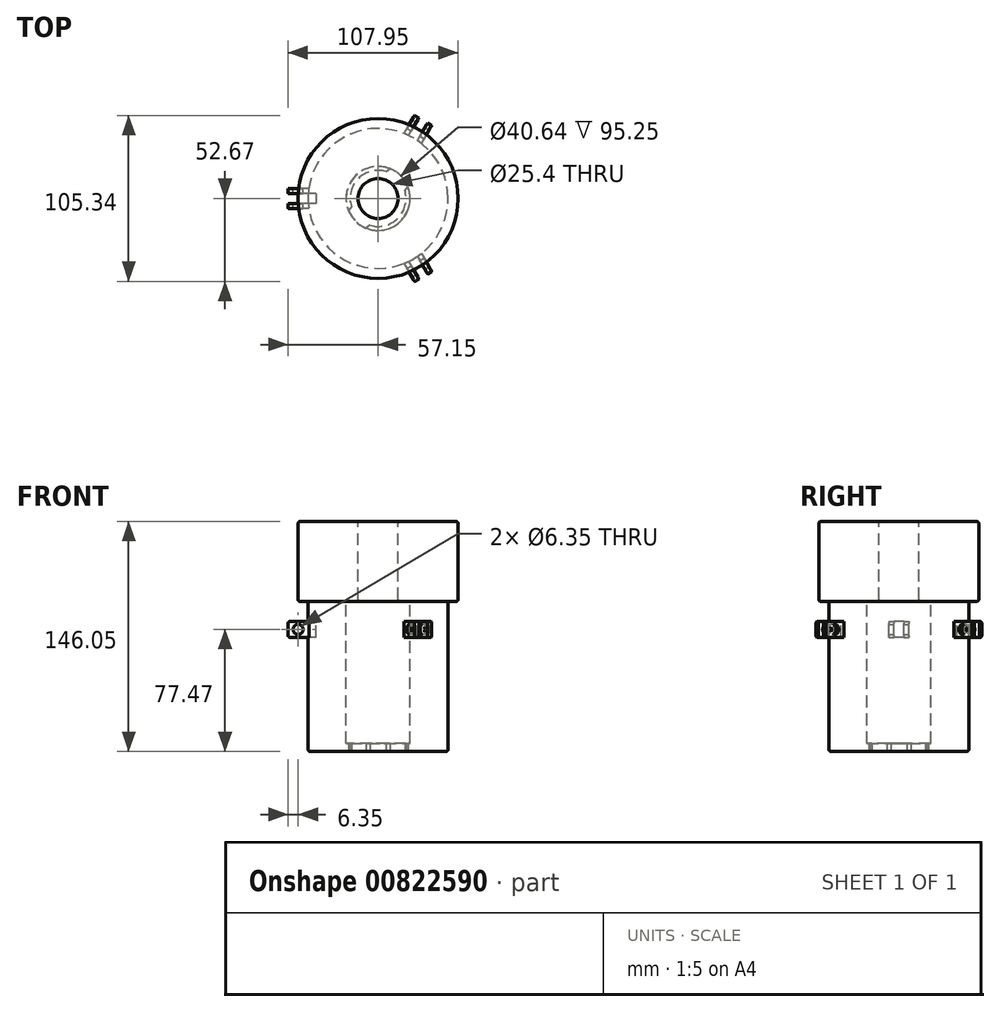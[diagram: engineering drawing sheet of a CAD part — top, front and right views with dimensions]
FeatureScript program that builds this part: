
annotation { "Feature Type Name" : "Feature", "Feature Type Description" : "" }
export const myFeature = defineFeature(function(context is Context, id is Id, definition is map)
    precondition{}
    {
        {
            var Q0;
            Q0=qCreatedBy(makeId("Top.planeOp"),FACE);
            var sketch = newSketch(context, id + "F0", { "sketchPlane" : qUnion([Q0])});
            skCircle(sketch, "E0", {"center": v(0, 0) * mm, "radius": 20.32 * mm});
            skCircle(sketch, "E1", {"center": v(0, 0) * mm, "radius": 44.45 * mm});
            skSolve(sketch);
        }
        {
            var Q0;
            Q0 = qSketchRegion(id + "F0", true);
            extrude(context, id + "F1", {"entities" : qUnion([Q0]), "oppositeDirection" : true, "depth" : 95.25 * mm, "offsetDistance" : 25.4 * mm});
        }
        {
            var Q0;
            Q0=makeQuery(id+"F0.imprint","IMPRINT",FACE,{"disambiguationData":[TD([[makeQuery(id+"F0.imprint","IMPRINT",EDGE,{"derivedFrom":sQuery(id+"F0.wireOp",EDGE,"E0")}),1.0]])]});
            var Q1;
            Q1=makeQuery(id+"F1.opExtrude","CAP_FACE",FACE,{"disambiguationData":[OSD([sQuery(id+"F0.wireOp",EDGE,"E0"),sQuery(id+"F0.wireOp",EDGE,"E1")])],"isStart":false});
            extrude(context, id + "F2", {"entities" : qUnion([Q0]), "operationType" : NewBodyOperationType.REMOVE, "depth" : 25.4 * mm, "endBoundEntityFace" : qUnion([Q1]), "offsetDistance" : 25.4 * mm});
        }
        {
            var Q0;
            {var subQ0=sQuery(id+"F0.wireOp",EDGE,"E0");Q0=makeQuery(id+"F2.boolean.opBoolean","MERGE",FACE,{"derivedFrom":[makeQuery(id+"F1.opExtrude","CAP_FACE",FACE,{"disambiguationData":[OSD([subQ0,sQuery(id+"F0.wireOp",EDGE,"E1")])],"isStart":true}),makeQuery(id+"F2.opExtrude","CAP_FACE",FACE,{"disambiguationData":[OSD([subQ0])],"isStart":true})]});}
            var sketch = newSketch(context, id + "F3", { "sketchPlane" : qUnion([Q0])});
            skCircle(sketch, "E2", {"center": v(0, 0) * mm, "radius": 50.8 * mm});
            skSolve(sketch);
        }
        {
            var Q0;
            Q0 = qSketchRegion(id + "F3", true);
            extrude(context, id + "F4", {"entities" : qUnion([Q0]), "operationType" : NewBodyOperationType.ADD, "depth" : 50.8 * mm, "offsetDistance" : 25.4 * mm});
        }
        {
            var Q0;
            Q0=makeQuery(id+"F4.opExtrude","SWEPT_FACE",FACE,{"disambiguationData":[OSD([sQuery(id+"F3.wireOp",EDGE,"E2")])]});
            fillet(context, id + "F5", {"entities" : qUnion([Q0]), "radius" : 1.27 * mm, "tangentPropagation" : true, "allowEdgeOverflow" : false});
        }
        {
            var Q0;
            Q0=makeQuery(id+"F1.opExtrude","CAP_EDGE",EDGE,{"disambiguationData":[OSD([sQuery(id+"F0.wireOp",EDGE,"E1")])],"isStart":false});
            fillet(context, id + "F6", {"entities" : qUnion([Q0]), "radius" : 1.27 * mm, "tangentPropagation" : true, "allowEdgeOverflow" : false});
        }
        {
            var Q0;
            Q0=makeQuery(id+"F4.opExtrude","CAP_FACE",FACE,{"disambiguationData":[OSD([sQuery(id+"F3.wireOp",EDGE,"E2")])],"isStart":false});
            var sketch = newSketch(context, id + "F7", { "sketchPlane" : qUnion([Q0])});
            skCircle(sketch, "E3", {"center": v(0, 0) * mm, "radius": 12.7 * mm});
            skSolve(sketch);
        }
        {
            var Q0;
            Q0=makeQuery(id+"F7.imprint","IMPRINT",FACE,{"disambiguationData":[TD([[makeQuery(id+"F7.imprint","IMPRINT",EDGE,{"derivedFrom":sQuery(id+"F7.wireOp",EDGE,"E3")}),1.0]])]});
            extrude(context, id + "F8", {"entities" : qUnion([Q0]), "operationType" : NewBodyOperationType.REMOVE, "oppositeDirection" : true, "depth" : 127 * mm, "offsetDistance" : 25.4 * mm});
        }
        {
            var Q0;
            Q0=makeQuery(id+"F8.boolean.opBoolean","COPY",FACE,{"derivedFrom":makeQuery(id+"F8.opExtrude","SWEPT_FACE",FACE,{"disambiguationData":[OSD([sQuery(id+"F7.wireOp",EDGE,"E3")])]})});
            fillet(context, id + "F9", {"entities" : qUnion([Q0]), "radius" : 1.27 * mm, "tangentPropagation" : true, "allowEdgeOverflow" : false});
        }
        {
            var Q0;
            Q0=qCreatedBy(makeId("Front.planeOp"),FACE);
            var sketch = newSketch(context, id + "F10", { "sketchPlane" : qUnion([Q0])});
            skLineSegment(sketch, "E4.bottom", {"start": v(-39.37, -22.86) * mm, "end": v(-55.88, -22.86) * mm});
            skLineSegment(sketch, "E4.top", {"start": v(-39.37, -12.7) * mm, "end": v(-55.88, -12.7) * mm});
            skLineSegment(sketch, "E4.left", {"start": v(-39.37, -22.86) * mm, "end": v(-39.37, -12.7) * mm});
            skLineSegment(sketch, "E4.right", {"start": v(-57.15, -21.6) * mm, "end": v(-57.15, -13.97) * mm});
            skPoint(sketch, "E5.visualSharp", {"position": v(-57.15, -22.86) * mm});
            skArc(sketch, "E5.filletArc", {"start": v(-57.15, -21.6) * mm, "mid": v(-56.78, -22.49) * mm, "end": v(-55.88, -22.86) * mm});
            skPoint(sketch, "E6.visualSharp", {"position": v(-57.15, -12.7) * mm});
            skArc(sketch, "E6.filletArc", {"start": v(-55.88, -12.7) * mm, "mid": v(-56.78, -13.07) * mm, "end": v(-57.15, -13.97) * mm});
            skCircle(sketch, "E7", {"center": v(-50.8, -17.78) * mm, "radius": 3.18 * mm});
            skSolve(sketch);
        }
        {
            var Q0;
            Q0 = qSketchRegion(id + "F10", true);
            extrude(context, id + "F11", {"entities" : qUnion([Q0]), "endBound" : BoundingType.SYMMETRIC, "depth" : 12.7 * mm, "offsetDistance" : 25.4 * mm});
        }
        {
            var Q0;
            Q0 = qSketchRegion(id + "F10", true);
            extrude(context, id + "F12", {"entities" : qUnion([Q0]), "operationType" : NewBodyOperationType.REMOVE, "endBound" : BoundingType.SYMMETRIC, "oppositeDirection" : true, "depth" : 6.35 * mm, "offsetDistance" : 25.4 * mm});
        }
        {
            var Q0;
            Q0=makeQuery(id+"F12.boolean.opBoolean","SPLIT",BODY,{"disambiguationData":[OD(0.0)],"derivedFrom":makeQuery(id+"F11.opExtrude","SWEPT_BODY",BODY,{"disambiguationData":[OSD([sQuery(id+"F10.wireOp",EDGE,"E4.bottom"),sQuery(id+"F10.wireOp",EDGE,"E4.top"),sQuery(id+"F10.wireOp",EDGE,"E4.left"),sQuery(id+"F10.wireOp",EDGE,"E4.right"),sQuery(id+"F10.wireOp",EDGE,"E5.filletArc"),sQuery(id+"F10.wireOp",EDGE,"E6.filletArc"),sQuery(id+"F10.wireOp",EDGE,"E7")])]})});
            var Q1;
            Q1=makeQuery(id+"F12.boolean.opBoolean","SPLIT",BODY,{"disambiguationData":[OD(1.0)],"derivedFrom":makeQuery(id+"F11.opExtrude","SWEPT_BODY",BODY,{"disambiguationData":[OSD([sQuery(id+"F10.wireOp",EDGE,"E4.bottom"),sQuery(id+"F10.wireOp",EDGE,"E4.top"),sQuery(id+"F10.wireOp",EDGE,"E4.left"),sQuery(id+"F10.wireOp",EDGE,"E4.right"),sQuery(id+"F10.wireOp",EDGE,"E5.filletArc"),sQuery(id+"F10.wireOp",EDGE,"E6.filletArc"),sQuery(id+"F10.wireOp",EDGE,"E7")])]})});
            var Q2;
            Q2=makeQuery(id+"F1.opExtrude","SWEPT_FACE",FACE,{"disambiguationData":[OSD([sQuery(id+"F0.wireOp",EDGE,"E1")])]});
            circularPattern(context, id + "F13", {"operationType" : NewBodyOperationType.ADD, "entities" : qUnion([Q0, Q1]), "axis" : qUnion([Q2]), "angle" : 360 * degree, "instanceCount" : 3, "equalSpace" : true});
        }
        {
            var Q0;
            Q0=makeQuery(id+"F1.opExtrude","CAP_FACE",FACE,{"disambiguationData":[OSD([sQuery(id+"F0.wireOp",EDGE,"E0"),sQuery(id+"F0.wireOp",EDGE,"E1")])],"isStart":false});
            var sketch = newSketch(context, id + "F14", { "sketchPlane" : qUnion([Q0])});
            skCircle(sketch, "E8", {"center": v(0, 0) * mm, "radius": 20.32 * mm});
            skCircle(sketch, "E9", {"center": v(0, 0) * mm, "radius": 17.78 * mm});
            skLineSegment(sketch, "E10", {"start": v(-5.08, 17.04) * mm, "end": v(-7.62, 18.84) * mm});
            skLineSegment(sketch, "E11", {"start": v(-17.04, 5.08) * mm, "end": v(-18.84, 7.62) * mm});
            skLineSegment(sketch, "E12", {"start": v(-14.37, 14.37) * mm, "end": v(0, 0) * mm, "construction": true});
            skLineSegment(sketch, "E13", {"start": v(-7.62, 18.84) * mm, "end": v(-14.37, 14.37) * mm, "construction": true});
            skLineSegment(sketch, "E14", {"start": v(-14.37, 14.37) * mm, "end": v(-18.84, 7.62) * mm, "construction": true});
            skLineSegment(sketch, "E15", {"start": v(-14.37, -14.37) * mm, "end": v(0, 0) * mm, "construction": true});
            skLineSegment(sketch, "E16", {"start": v(0, 0) * mm, "end": v(12.57, 12.57) * mm, "construction": true});
            skLineSegment(sketch, "E17.MirrorCS", {"start": v(17.04, -5.08) * mm, "end": v(18.84, -7.62) * mm});
            skLineSegment(sketch, "E18.MirrorCS", {"start": v(5.08, -17.04) * mm, "end": v(7.62, -18.84) * mm});
            skSolve(sketch);
        }
        {
            var Q0;
            {var subQ0=sQuery(id+"F14.wireOp",EDGE,"E10");Q0=makeQuery(id+"F14.imprint","IMPRINT",FACE,{"disambiguationData":[TD([[makeQuery(id+"F14.imprint","IMPRINT",EDGE,{"derivedFrom":subQ0}),-1.0]])]});}
            var Q1;
            {var subQ0=sQuery(id+"F14.wireOp",EDGE,"E11");Q1=makeQuery(id+"F14.imprint","IMPRINT",FACE,{"disambiguationData":[TD([[makeQuery(id+"F14.imprint","IMPRINT",EDGE,{"derivedFrom":subQ0}),1.0]])]});}
            extrude(context, id + "F15", {"entities" : qUnion([Q0, Q1]), "operationType" : NewBodyOperationType.ADD, "oppositeDirection" : true, "depth" : 5.08 * mm, "offsetDistance" : 25.4 * mm});
        }
    });
